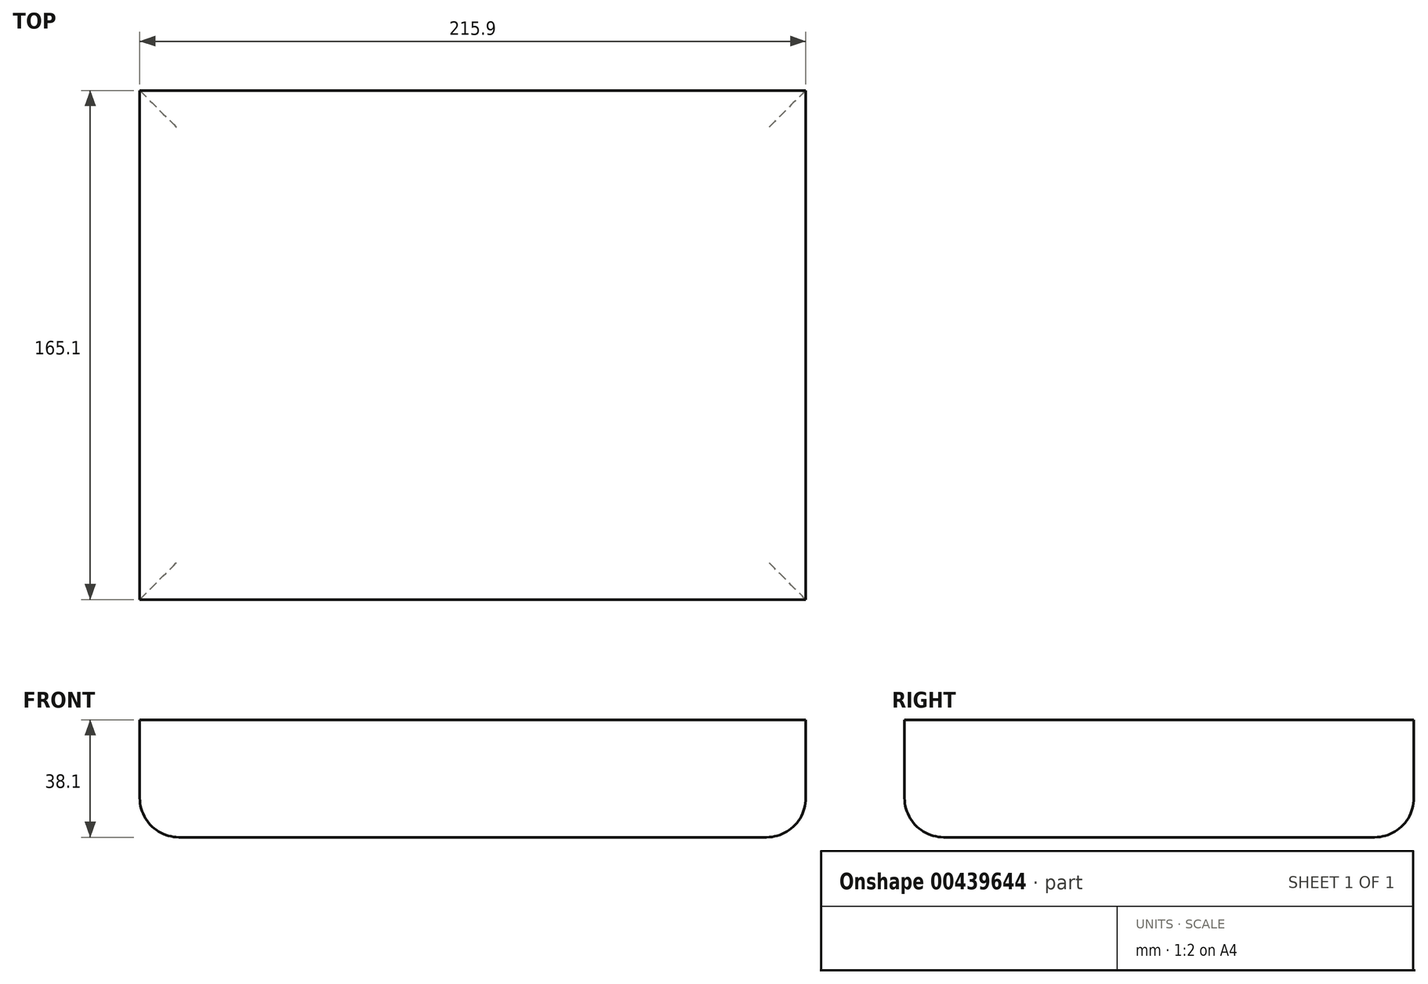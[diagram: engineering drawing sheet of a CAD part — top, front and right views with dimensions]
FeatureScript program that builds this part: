
annotation { "Feature Type Name" : "Feature", "Feature Type Description" : "" }
export const myFeature = defineFeature(function(context is Context, id is Id, definition is map)
    precondition{}
    {
        {
            var Q0;
            Q0=qCreatedBy(makeId("Top.planeOp"),FACE);
            var sketch = newSketch(context, id + "F0", { "sketchPlane" : qUnion([Q0])});
            skLineSegment(sketch, "E0.bottom", {"start": v(-107.95, 82.55) * mm, "end": v(107.95, 82.55) * mm});
            skLineSegment(sketch, "E0.top", {"start": v(-107.95, -82.55) * mm, "end": v(107.95, -82.55) * mm});
            skLineSegment(sketch, "E0.left", {"start": v(-107.95, 82.55) * mm, "end": v(-107.95, -82.55) * mm});
            skLineSegment(sketch, "E0.right", {"start": v(107.95, 82.55) * mm, "end": v(107.95, -82.55) * mm});
            skPoint(sketch, "E0.middle", {"position": v(0, 0) * mm});
            skSolve(sketch);
        }
        {
            var Q0;
            Q0 = qSketchRegion(id + "F0", true);
            extrude(context, id + "F1", {"entities" : qUnion([Q0]), "depth" : 38.1 * mm});
        }
        {
            var Q0;
            Q0=makeQuery(id+"F1.opExtrude","CAP_EDGE",EDGE,{"disambiguationData":[OSD([sQuery(id+"F0.wireOp",EDGE,"E0.top")])],"isStart":true});
            var Q1;
            Q1=makeQuery(id+"F1.opExtrude","CAP_EDGE",EDGE,{"disambiguationData":[OSD([sQuery(id+"F0.wireOp",EDGE,"E0.bottom")])],"isStart":true});
            var Q2;
            Q2=makeQuery(id+"F1.opExtrude","CAP_EDGE",EDGE,{"disambiguationData":[OSD([sQuery(id+"F0.wireOp",EDGE,"E0.left")])],"isStart":true});
            var Q3;
            Q3=makeQuery(id+"F1.opExtrude","CAP_EDGE",EDGE,{"disambiguationData":[OSD([sQuery(id+"F0.wireOp",EDGE,"E0.right")])],"isStart":true});
            fillet(context, id + "F2", {"entities" : qUnion([Q0, Q1, Q2, Q3]), "radius" : 12.7 * mm, "tangentPropagation" : true, "allowEdgeOverflow" : false});
        }
    });
